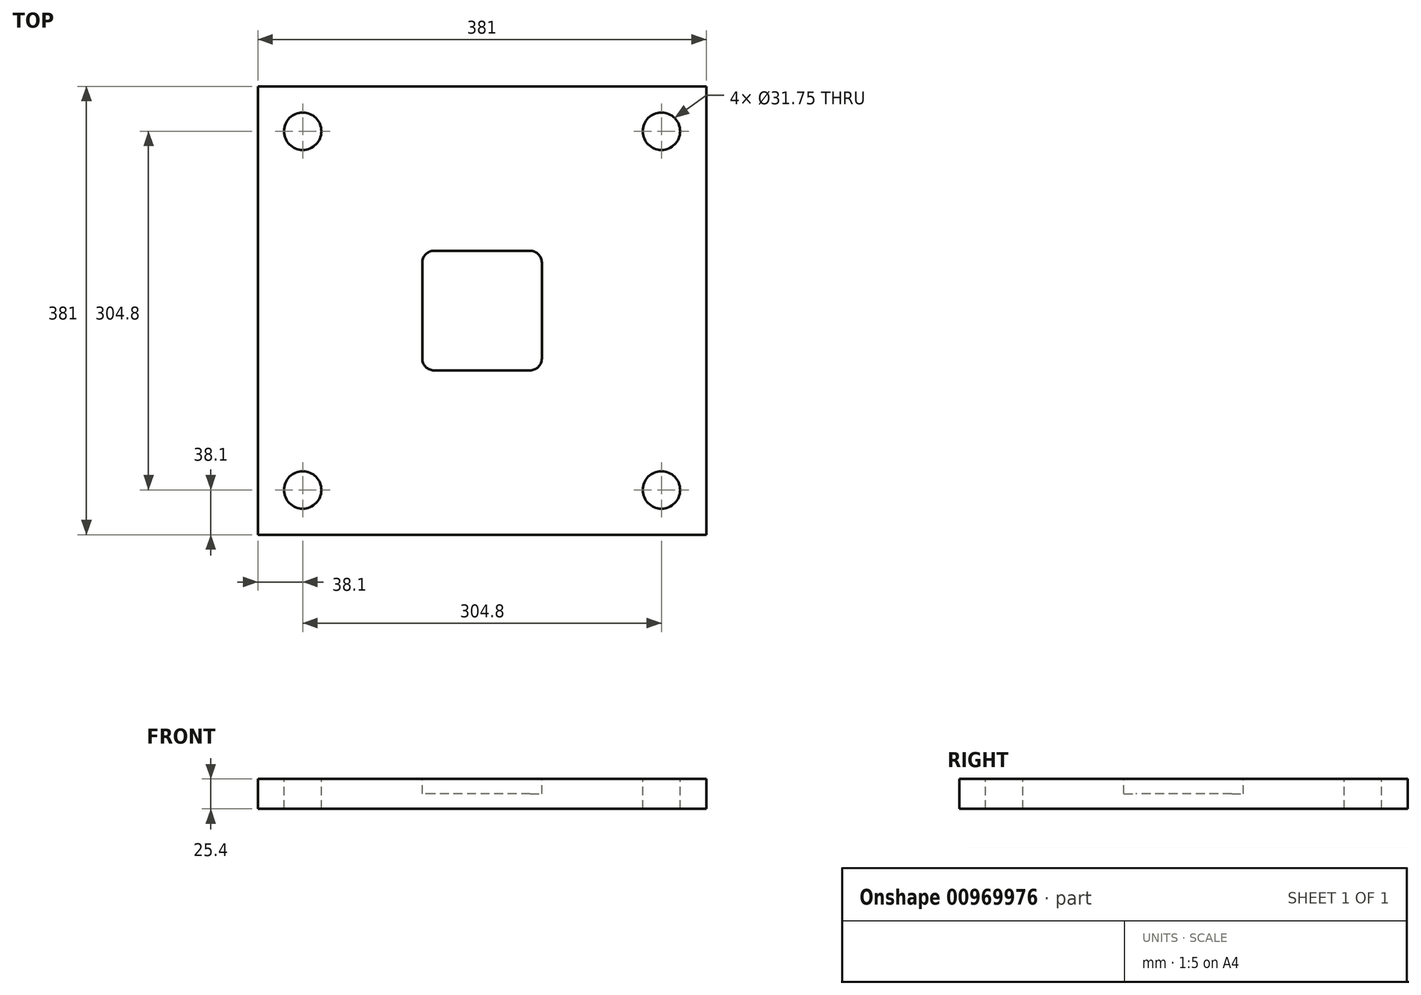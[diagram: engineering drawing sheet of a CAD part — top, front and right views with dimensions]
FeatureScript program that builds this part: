
annotation { "Feature Type Name" : "Feature", "Feature Type Description" : "" }
export const myFeature = defineFeature(function(context is Context, id is Id, definition is map)
    precondition{}
    {
        {
            var Q0;
            Q0=qCreatedBy(makeId("Top.planeOp"),FACE);
            var sketch = newSketch(context, id + "F0", { "sketchPlane" : qUnion([Q0])});
            skLineSegment(sketch, "E0.bottom", {"start": v(190.5, 190.5) * mm, "end": v(-190.5, 190.5) * mm});
            skLineSegment(sketch, "E0.top", {"start": v(190.5, -190.5) * mm, "end": v(-190.5, -190.5) * mm});
            skLineSegment(sketch, "E0.left", {"start": v(190.5, 190.5) * mm, "end": v(190.5, -190.5) * mm});
            skLineSegment(sketch, "E0.right", {"start": v(-190.5, 190.5) * mm, "end": v(-190.5, -190.5) * mm});
            skPoint(sketch, "E0.middle", {"position": v(0, 0) * mm});
            skSolve(sketch);
        }
        {
            var Q0;
            Q0 = qSketchRegion(id + "F0", true);
            extrude(context, id + "F1", {"entities" : qUnion([Q0]), "depth" : 25.4 * mm, "offsetDistance" : 25 * mm});
        }
        {
            var Q0;
            Q0=makeQuery(id+"F1.opExtrude","CAP_FACE",FACE,{"disambiguationData":[OSD([sQuery(id+"F0.wireOp",EDGE,"E0.bottom"),sQuery(id+"F0.wireOp",EDGE,"E0.top"),sQuery(id+"F0.wireOp",EDGE,"E0.left"),sQuery(id+"F0.wireOp",EDGE,"E0.right")])],"isStart":false});
            var sketch = newSketch(context, id + "F2", { "sketchPlane" : qUnion([Q0])});
            skLineSegment(sketch, "E1.bottom", {"start": v(50.8, 50.8) * mm, "end": v(-50.8, 50.8) * mm});
            skLineSegment(sketch, "E1.top", {"start": v(50.8, -50.8) * mm, "end": v(-50.8, -50.8) * mm});
            skLineSegment(sketch, "E1.left", {"start": v(50.8, 50.8) * mm, "end": v(50.8, -50.8) * mm});
            skLineSegment(sketch, "E1.right", {"start": v(-50.8, 50.8) * mm, "end": v(-50.8, -50.8) * mm});
            skPoint(sketch, "E1.middle", {"position": v(0, 0) * mm});
            skSolve(sketch);
        }
        {
            var Q0;
            Q0=makeQuery(id+"F2.imprint","IMPRINT",FACE,{"disambiguationData":[TD([[makeQuery(id+"F2.imprint","IMPRINT",EDGE,{"derivedFrom":sQuery(id+"F2.wireOp",EDGE,"E1.bottom")}),1.0]])]});
            extrude(context, id + "F3", {"entities" : qUnion([Q0]), "operationType" : NewBodyOperationType.REMOVE, "oppositeDirection" : true, "depth" : 12.7 * mm, "offsetDistance" : 25 * mm});
        }
        {
            var Q0;
            Q0=makeQuery(id+"F3.boolean.opBoolean","COPY",EDGE,{"derivedFrom":makeQuery(id+"F3.opExtrude","SWEPT_EDGE",EDGE,{"disambiguationData":[OSD([sQuery(id+"F2.wireOp",EDGE,"E1.bottom"),sQuery(id+"F2.wireOp",EDGE,"E1.left")])]})});
            var Q1;
            Q1=makeQuery(id+"F3.boolean.opBoolean","COPY",EDGE,{"derivedFrom":makeQuery(id+"F3.opExtrude","SWEPT_EDGE",EDGE,{"disambiguationData":[OSD([sQuery(id+"F2.wireOp",EDGE,"E1.bottom"),sQuery(id+"F2.wireOp",EDGE,"E1.right")])]})});
            var Q2;
            Q2=makeQuery(id+"F3.boolean.opBoolean","COPY",EDGE,{"derivedFrom":makeQuery(id+"F3.opExtrude","SWEPT_EDGE",EDGE,{"disambiguationData":[OSD([sQuery(id+"F2.wireOp",EDGE,"E1.top"),sQuery(id+"F2.wireOp",EDGE,"E1.right")])]})});
            var Q3;
            Q3=makeQuery(id+"F3.boolean.opBoolean","COPY",EDGE,{"derivedFrom":makeQuery(id+"F3.opExtrude","SWEPT_EDGE",EDGE,{"disambiguationData":[OSD([sQuery(id+"F2.wireOp",EDGE,"E1.top"),sQuery(id+"F2.wireOp",EDGE,"E1.left")])]})});
            fillet(context, id + "F4", {"entities" : qUnion([Q0, Q1, Q2, Q3]), "radius" : 10 * mm, "tangentPropagation" : true, "allowEdgeOverflow" : false});
        }
        {
            var Q0;
            Q0=makeQuery(id+"F1.opExtrude","CAP_FACE",FACE,{"disambiguationData":[OSD([sQuery(id+"F0.wireOp",EDGE,"E0.bottom"),sQuery(id+"F0.wireOp",EDGE,"E0.top"),sQuery(id+"F0.wireOp",EDGE,"E0.left"),sQuery(id+"F0.wireOp",EDGE,"E0.right")])],"isStart":false});
            var sketch = newSketch(context, id + "F5", { "sketchPlane" : qUnion([Q0])});
            skCircle(sketch, "E2", {"center": v(-152.4, 152.4) * mm, "radius": 15.88 * mm});
            skCircle(sketch, "E3", {"center": v(152.4, 152.4) * mm, "radius": 15.88 * mm});
            skCircle(sketch, "E4", {"center": v(152.4, -152.4) * mm, "radius": 15.88 * mm});
            skCircle(sketch, "E5", {"center": v(-152.4, -152.4) * mm, "radius": 15.88 * mm});
            skSolve(sketch);
        }
        {
            var Q0;
            Q0=makeQuery(id+"F5.imprint","IMPRINT",FACE,{"disambiguationData":[TD([[makeQuery(id+"F5.imprint","IMPRINT",EDGE,{"derivedFrom":sQuery(id+"F5.wireOp",EDGE,"E5")}),1.0]])]});
            var Q1;
            Q1=makeQuery(id+"F5.imprint","IMPRINT",FACE,{"disambiguationData":[TD([[makeQuery(id+"F5.imprint","IMPRINT",EDGE,{"derivedFrom":sQuery(id+"F5.wireOp",EDGE,"E2")}),1.0]])]});
            var Q2;
            Q2=makeQuery(id+"F5.imprint","IMPRINT",FACE,{"disambiguationData":[TD([[makeQuery(id+"F5.imprint","IMPRINT",EDGE,{"derivedFrom":sQuery(id+"F5.wireOp",EDGE,"E4")}),1.0]])]});
            var Q3;
            Q3=makeQuery(id+"F5.imprint","IMPRINT",FACE,{"disambiguationData":[TD([[makeQuery(id+"F5.imprint","IMPRINT",EDGE,{"derivedFrom":sQuery(id+"F5.wireOp",EDGE,"E3")}),1.0]])]});
            extrude(context, id + "F6", {"entities" : qUnion([Q0, Q1, Q2, Q3]), "operationType" : NewBodyOperationType.REMOVE, "oppositeDirection" : true, "depth" : 50 * mm, "offsetDistance" : 25 * mm});
        }
    });
